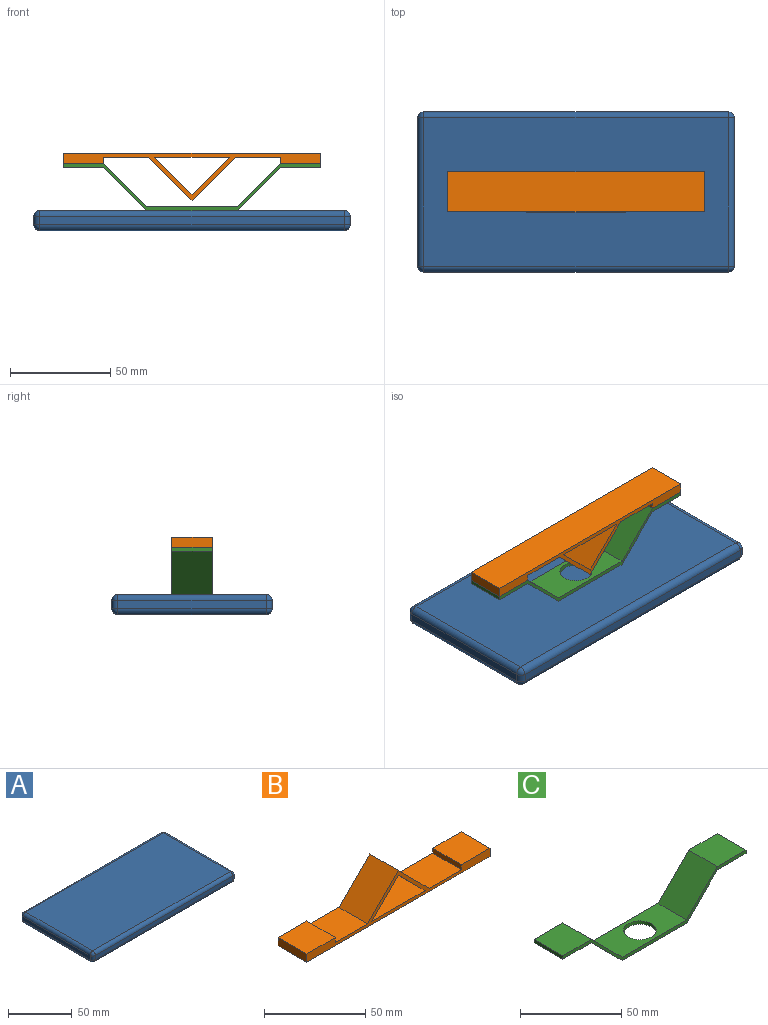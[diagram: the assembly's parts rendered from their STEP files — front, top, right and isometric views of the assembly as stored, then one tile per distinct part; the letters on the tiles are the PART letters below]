
ASSEMBLY  parts=3 mates=2
PART A: 26 faces, bbox 158x80x10 mm
  f0: plane 74x4mm, normal (-1,0,0), area 296mm2, adj f14,f19,f22,f25
  f1: plane 152x4mm, normal (0,-1,0), area 608mm2, adj f11,f20,f21,f25
  f2: plane 74x4mm, normal (1,0,0), area 296mm2, adj f6,f10,f11,f12
  f3: plane 152x4mm, normal (0,1,0), area 608mm2, adj f6,f9,f13,f14
  f4: plane 152x74mm, normal (0,0,1), area 11248mm2, adj f9,f10,f19,f20
  f5: plane 152x74mm, normal (0,0,-1), area 11248mm2, adj f12,f13,f21,f22
  f6: cylinder r=3mm len=4mm, axis (0,0,1), area 18.8mm2, adj f2,f3,f7,f8
  f7: sphere r=3mm, area 14.1mm2, adj f6,f9,f10
  f8: sphere r=3mm, area 14.1mm2, adj f6,f12,f13
  f9: cylinder r=3mm len=152mm, axis (1,0,0), area 716.3mm2, adj f3,f4,f7,f15
  f10: cylinder r=3mm len=74mm, axis (0,-1,0), area 348.7mm2, adj f2,f4,f7,f16
  f11: cylinder r=3mm len=4mm, axis (0,0,-1), area 18.8mm2, adj f1,f2,f16,f17
  f12: cylinder r=3mm len=74mm, axis (0,1,0), area 348.7mm2, adj f2,f5,f8,f17
  f13: cylinder r=3mm len=152mm, axis (-1,0,0), area 716.3mm2, adj f3,f5,f8,f18
  f14: cylinder r=3mm len=4mm, axis (0,0,-1), area 18.8mm2, adj f0,f3,f15,f18
  f15: sphere r=3mm, area 14.1mm2, adj f9,f14,f19
  f16: sphere r=3mm, area 14.1mm2, adj f10,f11,f20
  f17: sphere r=3mm, area 14.1mm2, adj f11,f12,f21
  f18: sphere r=3mm, area 14.1mm2, adj f13,f14,f22
  f19: cylinder r=3mm len=74mm, axis (0,1,0), area 348.7mm2, adj f0,f4,f15,f23
  f20: cylinder r=3mm len=152mm, axis (-1,0,0), area 716.3mm2, adj f1,f4,f16,f23
  f21: cylinder r=3mm len=152mm, axis (1,0,0), area 716.3mm2, adj f1,f5,f17,f24
  f22: cylinder r=3mm len=74mm, axis (0,-1,0), area 348.7mm2, adj f0,f5,f18,f24
  f23: sphere r=3mm, area 14.1mm2, adj f19,f20,f25
  f24: sphere r=3mm, area 14.1mm2, adj f21,f22,f25
  f25: cylinder r=3mm len=4mm, axis (0,0,1), area 18.8mm2, adj f0,f1,f23,f24
PART B: 16 faces, bbox 128x20x23.5 mm
  f0: plane 22.5x20mm, normal (0,0,1), area 450mm2, adj f3,f5,f9,f12
  f1: plane 37.34x20mm, normal (0,0,1), area 746.9mm2, adj f3,f5,f10,f11
  f2: plane 22.5x20mm, normal (0,0,1), area 450mm2, adj f3,f5,f8,f14
  f3: plane 128x23.5mm, normal (0,1,0), area 489.6mm2, adj f0,f1,f2,f4,f6,f7,f8,f9
  f4: plane 20x5mm, normal (-1,0,0), area 100mm2, adj f3,f5,f7,f13
  f5: plane 128x23.5mm, normal (0,-1,0), area 489.6mm2, adj f0,f1,f2,f4,f6,f7,f8,f9
  f6: plane 20x5mm, normal (1,0,0), area 100mm2, adj f3,f5,f7,f15
  f7: plane 128x20mm, normal (0,0,-1), area 2560mm2, adj f3,f4,f5,f6
  f8: plane 21.5x21.5mm, normal (0.71,0,0.71), area 608.1mm2, adj f2,f3,f5,f9
  f9: plane 21.5x21.5mm, normal (-0.71,0,0.71), area 608.1mm2, adj f0,f3,f5,f8
  f10: plane 20x18.67mm, normal (0.71,0,-0.71), area 528.1mm2, adj f1,f3,f5,f11
  f11: plane 20x18.67mm, normal (-0.71,0,-0.71), area 528.1mm2, adj f1,f3,f5,f10
  f12: plane 20x3mm, normal (1,0,0), area 60mm2, adj f0,f3,f5,f13
  f13: plane 20x20mm, normal (0,0,1), area 400mm2, adj f3,f4,f5,f12
  f14: plane 20x3mm, normal (-1,0,0), area 60mm2, adj f2,f3,f5,f15
  f15: plane 20x20mm, normal (0,0,1), area 400mm2, adj f3,f5,f6,f14
PART C: 15 faces, bbox 128x20x23.5 mm
  f0: plane 128x23.5mm, normal (0,1,0), area 256mm2, adj f3,f4,f5,f6,f7,f8,f9,f10
  f1: plane 128x23.5mm, normal (0,-1,0), area 256mm2, adj f3,f4,f5,f6,f7,f8,f9,f10
  f2: cylinder r=8mm len=16mm, axis (0,0,-1), area 100.5mm2, adj f3,f4
  f3: plane 45x20mm, normal (0,0,1), area 698.9mm2, adj f0,f1,f2,f5,f7
  f4: plane 45x20mm, normal (0,0,-1), area 698.9mm2, adj f0,f1,f2,f6,f8
  f5: plane 21.5x21.5mm, normal (0.71,0,0.71), area 608.1mm2, adj f0,f1,f3,f9
  f6: plane 21.5x21.5mm, normal (-0.71,0,-0.71), area 608.1mm2, adj f0,f1,f4,f10
  f7: plane 21.5x21.5mm, normal (-0.71,0,0.71), area 608.1mm2, adj f0,f1,f3,f13
  f8: plane 21.5x21.5mm, normal (0.71,0,-0.71), area 608.1mm2, adj f0,f1,f4,f12
  f9: plane 20x20mm, normal (0,0,1), area 400mm2, adj f0,f1,f5,f11
  f10: plane 20x20mm, normal (0,0,-1), area 400mm2, adj f0,f1,f6,f11
  f11: plane 20x2mm, normal (-1,0,0), area 40mm2, adj f0,f1,f9,f10
  f12: plane 20x20mm, normal (0,0,-1), area 400mm2, adj f0,f1,f8,f14
  f13: plane 20x20mm, normal (0,0,1), area 400mm2, adj f0,f1,f7,f14
  f14: plane 20x2mm, normal (1,0,0), area 40mm2, adj f0,f1,f12,f13
PLACE A t=(-29.65,-8.02,-10)mm
PLACE B rot(axis=(1,0,0),180deg) t=(8.44,-46.06,28.5)mm
PLACE C at identity
MATE fastened C.f11 <-> B.f4  axis (-1,0,0) through (-64,0,23.5)mm
MATE fastened C.f2 <-> A.f4  axis (0,0,-1) through (0,0,0)mm
